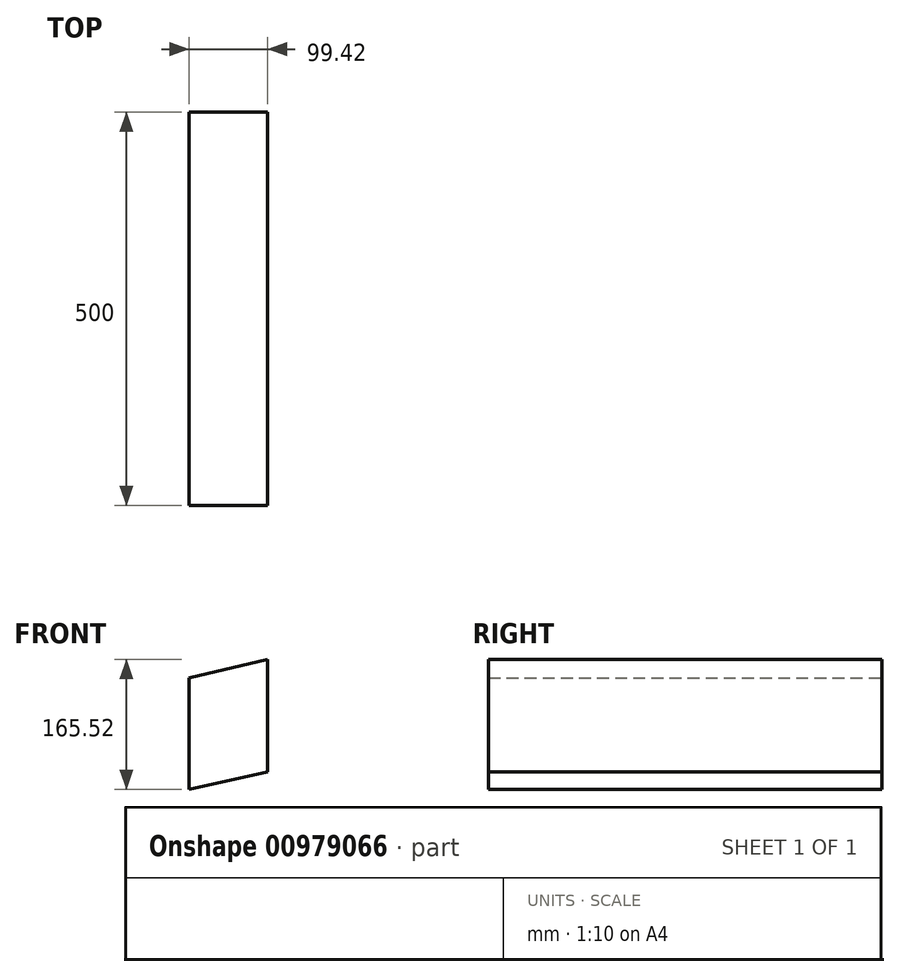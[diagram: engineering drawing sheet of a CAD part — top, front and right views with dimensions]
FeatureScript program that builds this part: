
annotation { "Feature Type Name" : "Feature", "Feature Type Description" : "" }
export const myFeature = defineFeature(function(context is Context, id is Id, definition is map)
    precondition{}
    {
        {
            var Q0;
            Q0=qCreatedBy(makeId("Front.planeOp"),FACE);
            var sketch = newSketch(context, id + "F0", { "sketchPlane" : qUnion([Q0])});
            skLineSegment(sketch, "E0", {"start": v(0, 0) * mm, "end": v(0, -120.87) * mm});
            skLineSegment(sketch, "E1", {"start": v(0, -120.87) * mm, "end": v(0, -141.62) * mm});
            skLineSegment(sketch, "E2", {"start": v(0, -141.62) * mm, "end": v(99.42, -119.18) * mm});
            skLineSegment(sketch, "E3", {"start": v(99.42, -119.18) * mm, "end": v(99.42, 23.9) * mm});
            skLineSegment(sketch, "E4", {"start": v(99.42, 23.9) * mm, "end": v(0, 0) * mm});
            skSolve(sketch);
        }
        {
            var Q0;
            Q0 = qSketchRegion(id + "F0", true);
            extrude(context, id + "F1", {"entities" : qUnion([Q0]), "depth" : 500 * mm, "offsetDistance" : 25 * mm});
        }
    });
